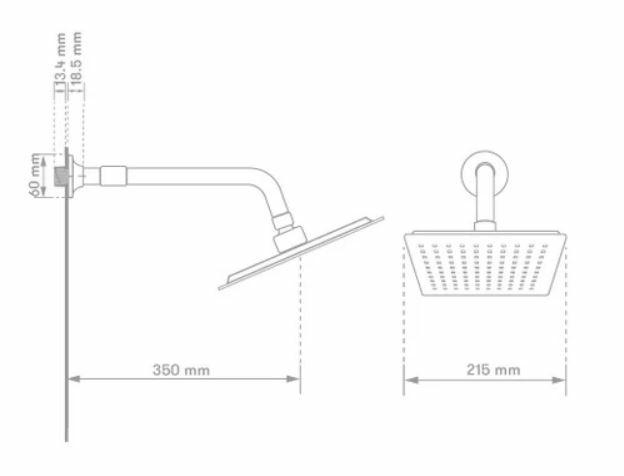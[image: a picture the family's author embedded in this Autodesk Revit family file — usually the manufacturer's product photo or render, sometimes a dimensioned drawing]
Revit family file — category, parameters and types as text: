
# Revit family: BL-8530-11-REGADERA VICO 10CM X 10CM
name_source: partatom
category: Plumbing Fixtures
revit_build: Autodesk Revit 2018 (Build: 20170223_1515(x64)
units: mm (PartAtom-declared; Revit-internal decimal feet)

## family parameters
Cut with Voids When Loaded = No
Host = Face
OmniClass Number = 23.31.11.00
Part Type = Normal
Room Calculation Point = No
Round Connector Dimension = Use Diameter
Shared = No

## types (1)
- BL-8530-11
    Alto = 100 mm  [stored 0.328084 ft]
    Ancho = 100 mm  [stored 0.328084 ft]
    CW Connection = Yes
    Default Elevation = 0 mm  [stored 0 ft]
    Description = Regadera
    HW Connection = Yes
    Link Ficha Tecnica = http://infotecnica.gricol.com
    Manufacturer = Gricol
    Model = BL-8530-11
    Plastico ABS Cromado = Plastico ABS Cromado
    Product Name = REGADERA VICO 10 cm x 10 cm
    Profundidad = 190 mm
    Type Image = REGADERA VICO FOTO.jpg
    URL = https://www.gricol.com
    Vent Connection = No
    Waste Connection = No

note: [stored X ft] marks values corroborated as IEEE doubles in the binary element streams (Revit-internal decimal feet)

## geometry (parser evidence)
native form markers: Blend x8, Sweep x21
no freeform markers — native parametric forms only
